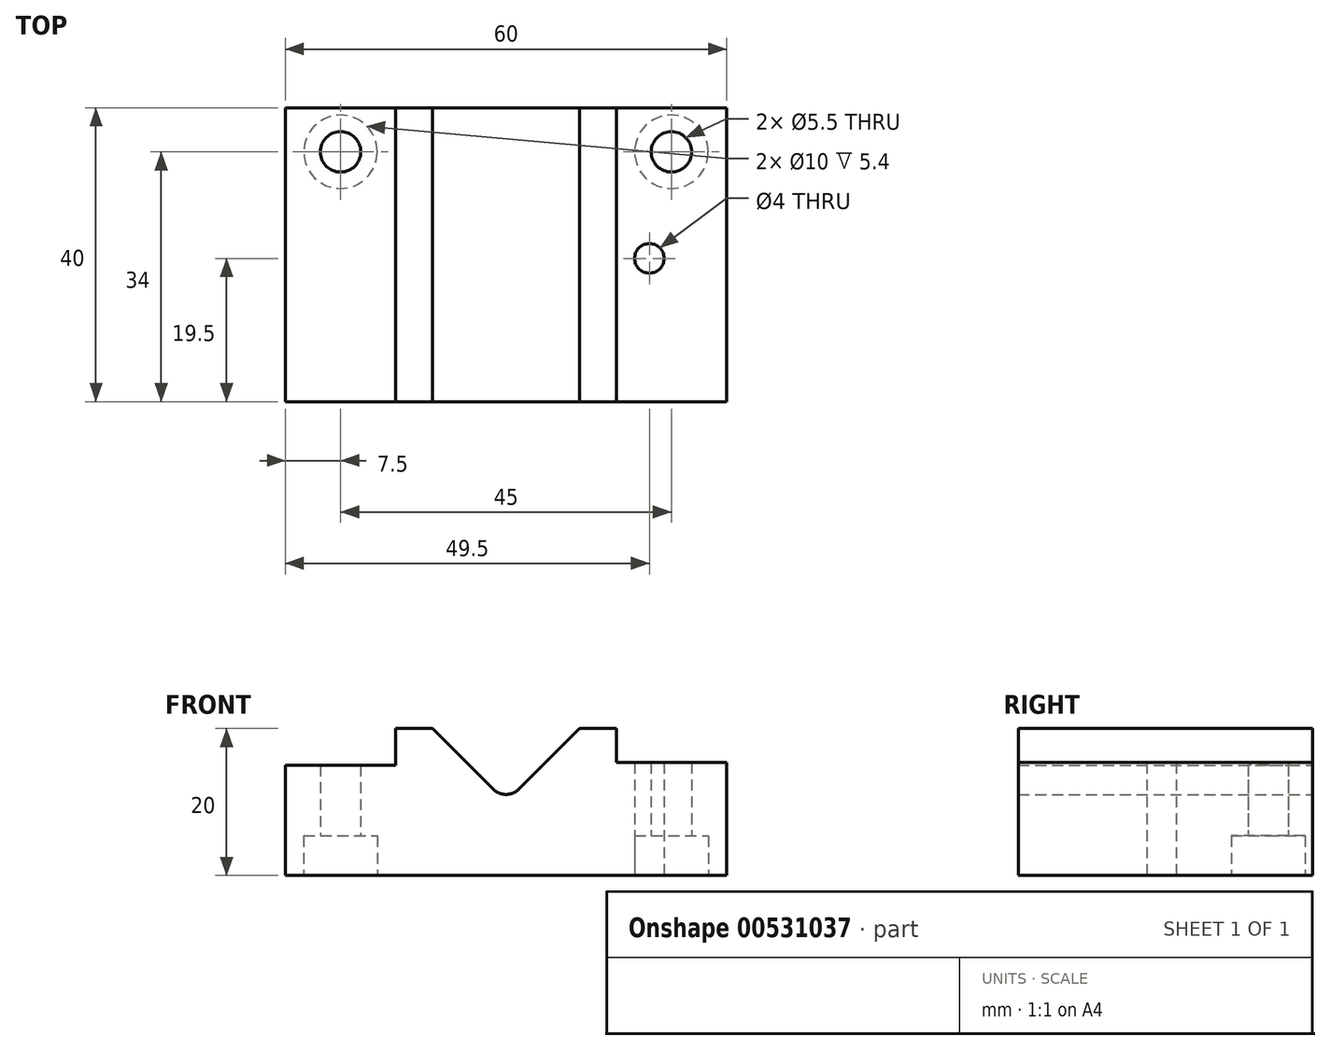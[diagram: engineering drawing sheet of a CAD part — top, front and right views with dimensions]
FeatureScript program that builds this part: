
annotation { "Feature Type Name" : "Feature", "Feature Type Description" : "" }
export const myFeature = defineFeature(function(context is Context, id is Id, definition is map)
    precondition{}
    {
        {
            var Q0;
            Q0=qCreatedBy(makeId("Front.planeOp"),FACE);
            var sketch = newSketch(context, id + "F0", { "sketchPlane" : qUnion([Q0])});
            skLineSegment(sketch, "E0", {"start": v(-30, 5) * mm, "end": v(-15, 5) * mm});
            skLineSegment(sketch, "E1", {"start": v(-15, 5) * mm, "end": v(-15, 10) * mm});
            skLineSegment(sketch, "E2", {"start": v(-15, 10) * mm, "end": v(-10, 10) * mm});
            skLineSegment(sketch, "E3", {"start": v(-10, 10) * mm, "end": v(-1.77, 1.77) * mm});
            skLineSegment(sketch, "E4", {"start": v(1.77, 1.77) * mm, "end": v(10, 10) * mm});
            skLineSegment(sketch, "E5", {"start": v(10, 10) * mm, "end": v(15, 10) * mm});
            skLineSegment(sketch, "E6", {"start": v(15, 10) * mm, "end": v(15, 5.36) * mm});
            skLineSegment(sketch, "E7", {"start": v(15, 5.36) * mm, "end": v(30, 5.36) * mm});
            skLineSegment(sketch, "E8", {"start": v(30, 5.36) * mm, "end": v(30, -10) * mm});
            skLineSegment(sketch, "E9", {"start": v(30, -10) * mm, "end": v(-30, -10) * mm});
            skLineSegment(sketch, "E10", {"start": v(-30, -10) * mm, "end": v(-30, 5) * mm});
            skPoint(sketch, "E11.visualSharp", {"position": v(0, 0) * mm});
            skArc(sketch, "E11.filletArc", {"start": v(-1.77, 1.77) * mm, "mid": v(0, 1.04) * mm, "end": v(1.77, 1.77) * mm});
            skSolve(sketch);
        }
        {
            var Q0;
            Q0=makeQuery(id+"F0.imprint","IMPRINT",FACE,{"disambiguationData":[TD([[makeQuery(id+"F0.imprint","IMPRINT",EDGE,{"derivedFrom":sQuery(id+"F0.wireOp",EDGE,"E0")}),-1.0]])]});
            extrude(context, id + "F1", {"entities" : qUnion([Q0]), "depth" : 40 * mm, "offsetDistance" : 25 * mm});
        }
        {
            var Q0;
            Q0=makeQuery(id+"F1.opExtrude","SWEPT_FACE",FACE,{"disambiguationData":[OSD([sQuery(id+"F0.wireOp",EDGE,"E9")])]});
            var sketch = newSketch(context, id + "F2", { "sketchPlane" : qUnion([Q0])});
            skPoint(sketch, "E12", {"position": v(-22.5, 6) * mm});
            skPoint(sketch, "E13", {"position": v(22.5, 6) * mm});
            skSolve(sketch);
        }
        {
            var Q0;
            Q0=sQuery(id+"F2.wireOp",VERTEX,"E12");
            var Q1;
            Q1=sQuery(id+"F2.wireOp",VERTEX,"E13");
            var Q2;
            Q2=makeQuery(id+"F1.opExtrude","SWEPT_BODY",BODY,{"disambiguationData":[OSD([sQuery(id+"F0.wireOp",EDGE,"E0"),sQuery(id+"F0.wireOp",EDGE,"E1"),sQuery(id+"F0.wireOp",EDGE,"E2"),sQuery(id+"F0.wireOp",EDGE,"E3"),sQuery(id+"F0.wireOp",EDGE,"E4"),sQuery(id+"F0.wireOp",EDGE,"E5"),sQuery(id+"F0.wireOp",EDGE,"E6"),sQuery(id+"F0.wireOp",EDGE,"E7"),sQuery(id+"F0.wireOp",EDGE,"E8"),sQuery(id+"F0.wireOp",EDGE,"E9"),sQuery(id+"F0.wireOp",EDGE,"E10"),sQuery(id+"F0.wireOp",EDGE,"E11.filletArc")])]});
            hole(context, id + "F3", {"style" : HoleStyle.C_BORE, "endStyle" : HoleEndStyle.THROUGH, "holeDiameter" : 5.5 * mm, "cBoreDiameter" : 10 * mm, "cBoreDepth" : 5.4 * mm, "isTappedThrough" : true, "tappedDepth" : 12 * mm, "tapClearance" : 3, "locations" : qUnion([Q0, Q1]), "scope" : qUnion([Q2])});
        }
        {
            var Q0;
            Q0=makeQuery(id+"F1.opExtrude","SWEPT_FACE",FACE,{"disambiguationData":[OSD([sQuery(id+"F0.wireOp",EDGE,"E9")])]});
            var sketch = newSketch(context, id + "F4", { "sketchPlane" : qUnion([Q0])});
            skPoint(sketch, "E14", {"position": v(19.5, 20.5) * mm});
            skSolve(sketch);
        }
        {
            var Q0;
            Q0=sQuery(id+"F4.wireOp",VERTEX,"E14");
            var Q1;
            Q1=makeQuery(id+"F1.opExtrude","SWEPT_BODY",BODY,{"disambiguationData":[OSD([sQuery(id+"F0.wireOp",EDGE,"E0"),sQuery(id+"F0.wireOp",EDGE,"E1"),sQuery(id+"F0.wireOp",EDGE,"E2"),sQuery(id+"F0.wireOp",EDGE,"E3"),sQuery(id+"F0.wireOp",EDGE,"E4"),sQuery(id+"F0.wireOp",EDGE,"E5"),sQuery(id+"F0.wireOp",EDGE,"E6"),sQuery(id+"F0.wireOp",EDGE,"E7"),sQuery(id+"F0.wireOp",EDGE,"E8"),sQuery(id+"F0.wireOp",EDGE,"E9"),sQuery(id+"F0.wireOp",EDGE,"E10"),sQuery(id+"F0.wireOp",EDGE,"E11.filletArc")])]});
            hole(context, id + "F5", {"style" : HoleStyle.SIMPLE, "endStyle" : HoleEndStyle.THROUGH, "holeDiameter" : 4 * mm, "isTappedThrough" : true, "tappedDepth" : 12 * mm, "tapClearance" : 3, "locations" : qUnion([Q0]), "scope" : qUnion([Q1])});
        }
    });
